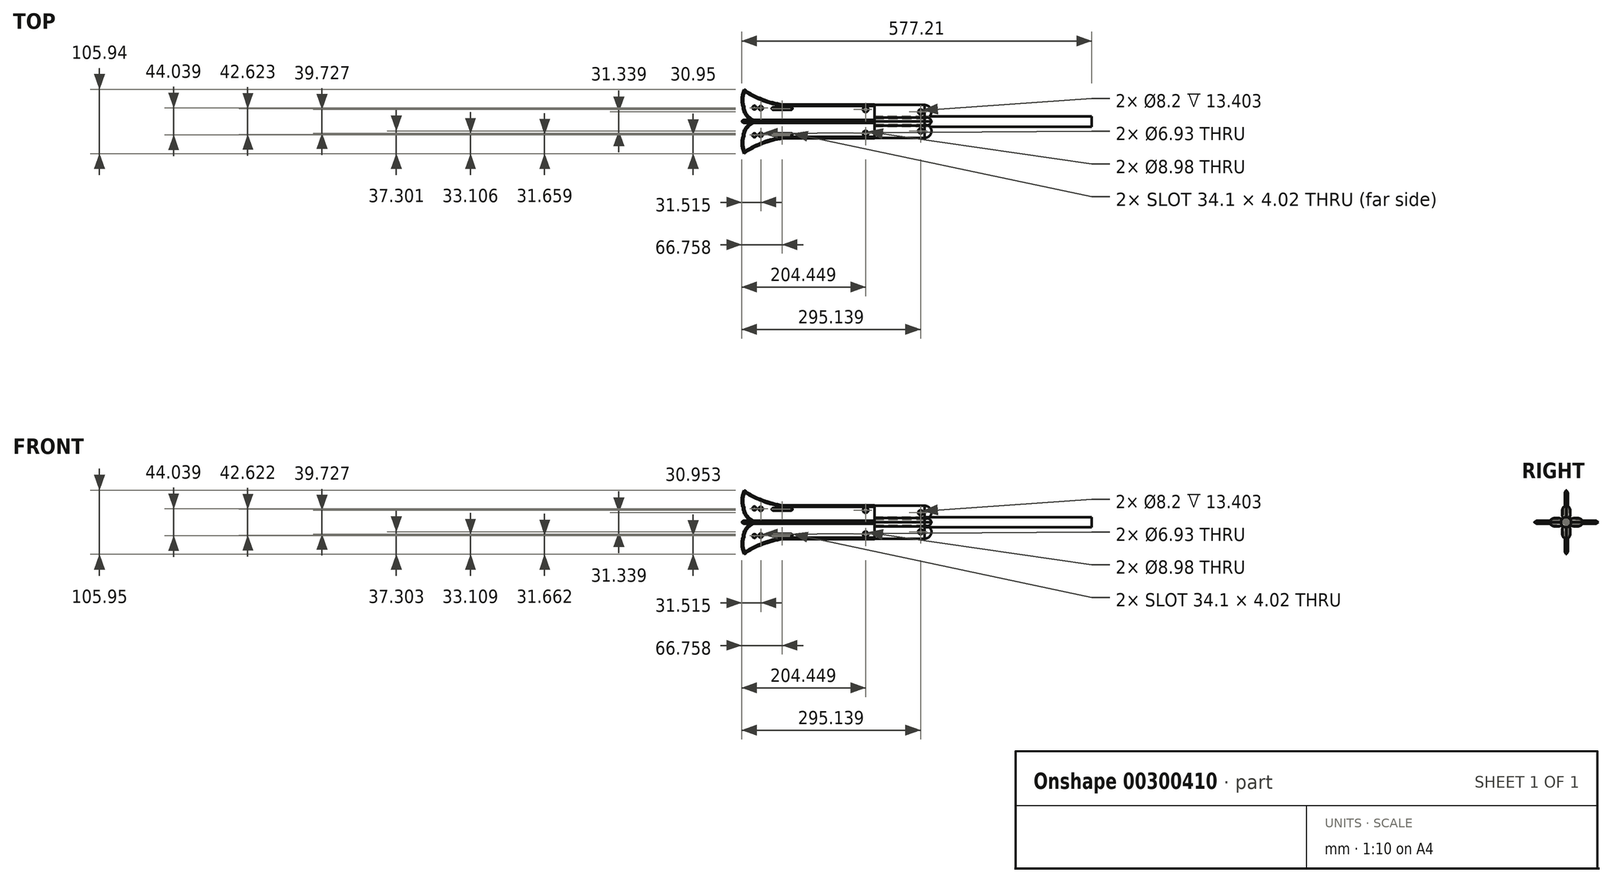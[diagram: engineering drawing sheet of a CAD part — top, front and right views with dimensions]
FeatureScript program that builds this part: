
annotation { "Feature Type Name" : "Feature", "Feature Type Description" : "" }
export const myFeature = defineFeature(function(context is Context, id is Id, definition is map)
    precondition{}
    {
        {
            var Q0;
            Q0=qCreatedBy(makeId("Right.planeOp"),FACE);
            var sketch = newSketch(context, id + "F0", { "sketchPlane" : qUnion([Q0])});
            skLineSegment(sketch, "E0.bottom", {"start": v(-6.7, 7.72) * mm, "end": v(6.7, 7.72) * mm});
            skLineSegment(sketch, "E0.top", {"start": v(-6.7, -15.03) * mm, "end": v(6.7, -15.03) * mm});
            skLineSegment(sketch, "E0.left", {"start": v(-6.7, 7.72) * mm, "end": v(-6.7, -15.03) * mm});
            skLineSegment(sketch, "E0.right", {"start": v(6.7, 7.72) * mm, "end": v(6.7, -15.03) * mm});
            skSolve(sketch);
        }
        {
            var Q0;
            Q0 = qSketchRegion(id + "F0", true);
            extrude(context, id + "F1", {"entities" : qUnion([Q0]), "depth" : 82.8 * mm});
        }
        {
            var Q0;
            Q0=makeQuery(id+"F1.opExtrude","SWEPT_EDGE",EDGE,{"disambiguationData":[OSD([sQuery(id+"F0.wireOp",EDGE,"E0.bottom"),sQuery(id+"F0.wireOp",EDGE,"E0.left")])]});
            var Q1;
            Q1=makeQuery(id+"F1.opExtrude","SWEPT_EDGE",EDGE,{"disambiguationData":[OSD([sQuery(id+"F0.wireOp",EDGE,"E0.bottom"),sQuery(id+"F0.wireOp",EDGE,"E0.right")])]});
            var Q2;
            Q2=makeQuery(id+"F1.opExtrude","SWEPT_EDGE",EDGE,{"disambiguationData":[OSD([sQuery(id+"F0.wireOp",EDGE,"E0.top"),sQuery(id+"F0.wireOp",EDGE,"E0.left")])]});
            var Q3;
            Q3=makeQuery(id+"F1.opExtrude","SWEPT_EDGE",EDGE,{"disambiguationData":[OSD([sQuery(id+"F0.wireOp",EDGE,"E0.top"),sQuery(id+"F0.wireOp",EDGE,"E0.right")])]});
            fillet(context, id + "F2", {"entities" : qUnion([Q0, Q1, Q2, Q3]), "radius" : 7.62 * mm, "tangentPropagation" : true, "allowEdgeOverflow" : false});
        }
        {
            var Q0;
            Q0=qCreatedBy(makeId("Front.planeOp"),FACE);
            var sketch = newSketch(context, id + "F3", { "sketchPlane" : qUnion([Q0])});
            skLineSegment(sketch, "E1.bottom", {"start": v(0, 12.24) * mm, "end": v(-217.44, 12.24) * mm});
            skLineSegment(sketch, "E1.top", {"start": v(0, -15.9) * mm, "end": v(-217.44, -15.9) * mm});
            skLineSegment(sketch, "E1.left", {"start": v(0, 12.24) * mm, "end": v(0, -15.9) * mm});
            skLineSegment(sketch, "E1.right", {"start": v(-217.44, 12.24) * mm, "end": v(-217.44, -15.9) * mm});
            skLineSegment(sketch, "E2", {"start": v(0, 7.72) * mm, "end": v(0, -11.37) * mm});
            skSolve(sketch);
        }
        {
            var Q0;
            Q0 = qSketchRegion(id + "F3", true);
            extrude(context, id + "F4", {"entities" : qUnion([Q0]), "endBound" : BoundingType.SYMMETRIC, "depth" : 5.08 * mm});
        }
        {
            var Q0;
            Q0=qCreatedBy(makeId("Front.planeOp"),FACE);
            var sketch = newSketch(context, id + "F5", { "sketchPlane" : qUnion([Q0])});
            skArc(sketch, "E3", {"start": v(-199.02, 12.52) * mm, "mid": v(-212.87, 1.53) * mm, "end": v(-217.44, -15.55) * mm});
            skLineSegment(sketch, "E4", {"start": v(-199.02, 12.52) * mm, "end": v(-199.02, 17.65) * mm});
            skLineSegment(sketch, "E5", {"start": v(-199.02, 17.65) * mm, "end": v(-217.44, 17.65) * mm});
            skLineSegment(sketch, "E6", {"start": v(-217.44, 17.65) * mm, "end": v(-217.44, -17.23) * mm});
            skLineSegment(sketch, "E7", {"start": v(-217.44, -17.23) * mm, "end": v(-217.44, -15.55) * mm});
            skSolve(sketch);
        }
        {
            var Q0;
            Q0 = qSketchRegion(id + "F5", true);
            extrude(context, id + "F6", {"entities" : qUnion([Q0]), "operationType" : NewBodyOperationType.REMOVE, "endBound" : BoundingType.SYMMETRIC, "oppositeDirection" : true, "depth" : 136.65 * mm});
        }
        {
            var Q0;
            Q0=qCreatedBy(makeId("Front.planeOp"),FACE);
            var sketch = newSketch(context, id + "F7", { "sketchPlane" : qUnion([Q0])});
            skCircle(sketch, "E8", {"center": v(76.07, -3.43) * mm, "radius": 4.1 * mm});
            skSolve(sketch);
        }
        {
            var Q0;
            Q0 = qSketchRegion(id + "F7", true);
            extrude(context, id + "F8", {"entities" : qUnion([Q0]), "operationType" : NewBodyOperationType.REMOVE, "endBound" : BoundingType.SYMMETRIC, "oppositeDirection" : true, "depth" : 25.4 * mm});
        }
        {
            var Q0;
            Q0=qCreatedBy(makeId("Front.planeOp"),FACE);
            var sketch = newSketch(context, id + "F9", { "sketchPlane" : qUnion([Q0])});
            skArc(sketch, "E9", {"start": v(82.82, -14.98) * mm, "mid": v(94.01, -3.74) * mm, "end": v(82.88, 7.56) * mm});
            skLineSegment(sketch, "E10", {"start": v(82.88, 7.56) * mm, "end": v(82.82, -14.98) * mm});
            skSolve(sketch);
        }
        {
            var Q0;
            Q0 = qSketchRegion(id + "F9", true);
            extrude(context, id + "F10", {"entities" : qUnion([Q0]), "operationType" : NewBodyOperationType.ADD, "endBound" : BoundingType.SYMMETRIC, "depth" : 12.7 * mm});
        }
        {
            var Q0;
            Q0=makeQuery(id+"F10.opExtrude","CAP_EDGE",EDGE,{"disambiguationData":[OSD([sQuery(id+"F9.wireOp",EDGE,"E9")])],"isStart":true});
            var Q1;
            Q1=makeQuery(id+"F10.opExtrude","CAP_EDGE",EDGE,{"disambiguationData":[OSD([sQuery(id+"F9.wireOp",EDGE,"E9")])],"isStart":false});
            fillet(context, id + "F11", {"entities" : qUnion([Q0, Q1]), "radius" : 7.62 * mm, "tangentPropagation" : true, "allowEdgeOverflow" : false});
        }
        {
            var Q0;
            Q0=qCreatedBy(makeId("Front.planeOp"),FACE);
            var sketch = newSketch(context, id + "F12", { "sketchPlane" : qUnion([Q0])});
            skCircle(sketch, "E11", {"center": v(-198.03, -10.53) * mm, "radius": 3.2 * mm});
            skLineSegment(sketch, "E12.bottom", {"start": v(-167.35, -7.06) * mm, "end": v(-137.27, -7.06) * mm});
            skLineSegment(sketch, "E12.top", {"start": v(-167.35, -11.08) * mm, "end": v(-137.27, -11.08) * mm});
            skLineSegment(sketch, "E12.left", {"start": v(-167.35, -7.06) * mm, "end": v(-167.35, -11.08) * mm});
            skLineSegment(sketch, "E12.right", {"start": v(-137.27, -7.06) * mm, "end": v(-137.27, -11.08) * mm});
            skArc(sketch, "E13", {"start": v(-137.27, -11.08) * mm, "mid": v(-135.26, -9.07) * mm, "end": v(-137.27, -7.06) * mm});
            skCircle(sketch, "E14", {"center": v(-187.55, -9.78) * mm, "radius": 3.47 * mm});
            skCircle(sketch, "E15", {"center": v(-14.62, -7.62) * mm, "radius": 4.49 * mm});
            skArc(sketch, "E16", {"start": v(-167.35, -7.06) * mm, "mid": v(-169.36, -9.07) * mm, "end": v(-167.35, -11.08) * mm});
            skSolve(sketch);
        }
        {
            var Q0;
            Q0=qCreatedBy(makeId("Front.planeOp"),FACE);
            var sketch = newSketch(context, id + "F13", { "sketchPlane" : qUnion([Q0])});
            skArc(sketch, "E17", {"start": v(-134.63, -14.4) * mm, "mid": v(-176.88, -21.85) * mm, "end": v(-215.4, -40.73) * mm});
            skArc(sketch, "E18", {"start": v(-200.65, 11.59) * mm, "mid": v(-217.48, -11.9) * mm, "end": v(-215.4, -40.73) * mm});
            skLineSegment(sketch, "E19", {"start": v(-200.65, 11.59) * mm, "end": v(-134.63, -14.4) * mm});
            skSolve(sketch);
        }
        {
            var Q0;
            Q0 = qSketchRegion(id + "F13", true);
            extrude(context, id + "F14", {"entities" : qUnion([Q0]), "operationType" : NewBodyOperationType.ADD, "endBound" : BoundingType.SYMMETRIC, "depth" : 5.08 * mm});
        }
        {
            var Q0;
            Q0 = qSketchRegion(id + "F12", true);
            extrude(context, id + "F15", {"entities" : qUnion([Q0]), "operationType" : NewBodyOperationType.REMOVE, "endBound" : BoundingType.SYMMETRIC, "depth" : 25.4 * mm});
        }
        {
            var Q0;
            Q0=makeQuery(id+"F14.opExtrude","CAP_EDGE",EDGE,{"disambiguationData":[OSD([sQuery(id+"F13.wireOp",EDGE,"E18")])],"isStart":true});
            var Q1;
            {var subQ0=sQuery(id+"F5.wireOp",EDGE,"E3");Q1=makeQuery(id+"F6.boolean.opBoolean","INTERSECT",EDGE,{"derivedFrom":[makeQuery(id+"F4.opExtrude","CAP_FACE",FACE,{"disambiguationData":[OSD([sQuery(id+"F3.wireOp",EDGE,"E1.bottom"),sQuery(id+"F3.wireOp",EDGE,"E1.top"),sQuery(id+"F3.wireOp",EDGE,"E1.left"),sQuery(id+"F3.wireOp",EDGE,"E1.right"),sQuery(id+"F3.wireOp",EDGE,"E2")])],"isStart":true}),makeQuery(id+"F6.opExtrude","SWEPT_FACE",FACE,{"disambiguationData":[OSD([subQ0]),TDD([makeQuery(id+"F5.imprint","IMPRINT",EDGE,{"disambiguationData":[TD([[makeQuery(id+"F5.imprint","INTERSECT",VERTEX,{"derivedFrom":[subQ0,sQuery(id+"F5.wireOp",EDGE,"E4")]}),-1.0]])],"derivedFrom":subQ0})])]})]});}
            var Q2;
            Q2=makeQuery(id+"F4.opExtrude","CAP_EDGE",EDGE,{"disambiguationData":[OSD([sQuery(id+"F3.wireOp",EDGE,"E1.top")])],"isStart":true});
            var Q3;
            Q3=makeQuery(id+"F4.opExtrude","CAP_EDGE",EDGE,{"disambiguationData":[OSD([sQuery(id+"F3.wireOp",EDGE,"E1.top")])],"isStart":false});
            var Q4;
            Q4=makeQuery(id+"F14.opExtrude","CAP_EDGE",EDGE,{"disambiguationData":[OSD([sQuery(id+"F13.wireOp",EDGE,"E17")])],"isStart":false});
            var Q5;
            Q5=makeQuery(id+"F14.opExtrude","CAP_EDGE",EDGE,{"disambiguationData":[OSD([sQuery(id+"F13.wireOp",EDGE,"E17")])],"isStart":true});
            var Q6;
            Q6=makeQuery(id+"F14.opExtrude","CAP_EDGE",EDGE,{"disambiguationData":[OSD([sQuery(id+"F13.wireOp",EDGE,"E18")])],"isStart":false});
            var Q7;
            {var subQ0=sQuery(id+"F5.wireOp",EDGE,"E3");Q7=makeQuery(id+"F6.boolean.opBoolean","INTERSECT",EDGE,{"derivedFrom":[makeQuery(id+"F4.opExtrude","CAP_FACE",FACE,{"disambiguationData":[OSD([sQuery(id+"F3.wireOp",EDGE,"E1.bottom"),sQuery(id+"F3.wireOp",EDGE,"E1.top"),sQuery(id+"F3.wireOp",EDGE,"E1.left"),sQuery(id+"F3.wireOp",EDGE,"E1.right"),sQuery(id+"F3.wireOp",EDGE,"E2")])],"isStart":false}),makeQuery(id+"F6.opExtrude","SWEPT_FACE",FACE,{"disambiguationData":[OSD([subQ0]),TDD([makeQuery(id+"F5.imprint","IMPRINT",EDGE,{"disambiguationData":[TD([[makeQuery(id+"F5.imprint","INTERSECT",VERTEX,{"derivedFrom":[subQ0,sQuery(id+"F5.wireOp",EDGE,"E4")]}),-1.0]])],"derivedFrom":subQ0})])]})]});}
            var Q8;
            Q8=makeQuery(id+"F4.opExtrude","CAP_EDGE",EDGE,{"disambiguationData":[OSD([sQuery(id+"F3.wireOp",EDGE,"E1.bottom")])],"isStart":false});
            var Q9;
            Q9=makeQuery(id+"F4.opExtrude","CAP_EDGE",EDGE,{"disambiguationData":[OSD([sQuery(id+"F3.wireOp",EDGE,"E1.bottom")])],"isStart":true});
            chamfer(context, id + "F16", {"entities" : qUnion([Q0, Q1, Q2, Q3, Q4, Q5, Q6, Q7, Q8, Q9]), "width" : 2.54 * mm, "tangentPropagation" : true});
        }
        {
            var Q0;
            Q0=makeQuery(id+"F1.opExtrude","SWEPT_BODY",BODY,{"disambiguationData":[OSD([sQuery(id+"F0.wireOp",EDGE,"E0.bottom"),sQuery(id+"F0.wireOp",EDGE,"E0.top"),sQuery(id+"F0.wireOp",EDGE,"E0.left"),sQuery(id+"F0.wireOp",EDGE,"E0.right")])]});
            var Q1;
            Q1=makeQuery(id+"F4.opExtrude","SWEPT_BODY",BODY,{"disambiguationData":[OSD([sQuery(id+"F3.wireOp",EDGE,"E1.bottom"),sQuery(id+"F3.wireOp",EDGE,"E1.top"),sQuery(id+"F3.wireOp",EDGE,"E1.left"),sQuery(id+"F3.wireOp",EDGE,"E1.right"),sQuery(id+"F3.wireOp",EDGE,"E2")])]});
            var Q2;
            Q2=makeQuery(id+"F10.opExtrude","SWEPT_BODY",BODY,{"disambiguationData":[OSD([sQuery(id+"F9.wireOp",EDGE,"E9"),sQuery(id+"F9.wireOp",EDGE,"E10")])]});
            var Q3;
            {var subQ0=sQuery(id+"F3.wireOp",EDGE,"E1.bottom");Q3=makeQuery(id+"F16.opChamfer","BLEND_FACE",FACE,{"disambiguationData":[OSD([subQ0]),TDD([makeQuery(id+"F4.opExtrude","CAP_EDGE",EDGE,{"disambiguationData":[OSD([subQ0])],"isStart":true})])]});}
            mirror(context, id + "F17", {"operationType" : NewBodyOperationType.ADD, "entities" : qUnion([Q0, Q1, Q2]), "mirrorPlane" : qUnion([Q3])});
        }
        {
            var Q0;
            Q0=makeQuery(id+"F4.opExtrude","SWEPT_BODY",BODY,{"disambiguationData":[OSD([sQuery(id+"F3.wireOp",EDGE,"E1.bottom"),sQuery(id+"F3.wireOp",EDGE,"E1.top"),sQuery(id+"F3.wireOp",EDGE,"E1.left"),sQuery(id+"F3.wireOp",EDGE,"E1.right"),sQuery(id+"F3.wireOp",EDGE,"E2")])]});
            var Q1;
            Q1=makeQuery(id+"F1.opExtrude","SWEPT_BODY",BODY,{"disambiguationData":[OSD([sQuery(id+"F0.wireOp",EDGE,"E0.bottom"),sQuery(id+"F0.wireOp",EDGE,"E0.top"),sQuery(id+"F0.wireOp",EDGE,"E0.left"),sQuery(id+"F0.wireOp",EDGE,"E0.right")])]});
            var Q2;
            Q2=makeQuery(id+"F17.opPattern","COPY",BODY,{"derivedFrom":makeQuery(id+"F10.opExtrude","SWEPT_BODY",BODY,{"disambiguationData":[OSD([sQuery(id+"F9.wireOp",EDGE,"E9"),sQuery(id+"F9.wireOp",EDGE,"E10")])]}),"instanceName":"1"});
            var Q3;
            Q3=makeQuery(id+"F10.opExtrude","SWEPT_BODY",BODY,{"disambiguationData":[OSD([sQuery(id+"F9.wireOp",EDGE,"E9"),sQuery(id+"F9.wireOp",EDGE,"E10")])]});
            var Q4;
            {var subQ0=sQuery(id+"F3.wireOp",EDGE,"E1.bottom");var subQ1=makeQuery(id+"F16.opChamfer","BLEND_FACE",FACE,{"disambiguationData":[OSD([subQ0]),TDD([makeQuery(id+"F4.opExtrude","CAP_EDGE",EDGE,{"disambiguationData":[OSD([subQ0])],"isStart":false})])]});Q4=makeQuery(id+"F17.boolean.opBoolean","MERGE",FACE,{"derivedFrom":[subQ1,makeQuery(id+"F17.opPattern","COPY",FACE,{"derivedFrom":subQ1,"instanceName":"1"})]});}
            mirror(context, id + "F18", {"operationType" : NewBodyOperationType.ADD, "entities" : qUnion([Q0, Q1, Q2, Q3]), "mirrorPlane" : qUnion([Q4])});
        }
        {
            var Q0;
            Q0=qCreatedBy(makeId("Right.planeOp"),FACE);
            var sketch = newSketch(context, id + "F19", { "sketchPlane" : qUnion([Q0])});
            skCircle(sketch, "E20", {"center": v(-0.42, 12.24) * mm, "radius": 8.46 * mm});
            skSolve(sketch);
        }
        {
            var Q0;
            Q0 = qSketchRegion(id + "F19", true);
            extrude(context, id + "F20", {"entities" : qUnion([Q0]), "depth" : 358.14 * mm});
        }
    });
